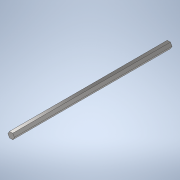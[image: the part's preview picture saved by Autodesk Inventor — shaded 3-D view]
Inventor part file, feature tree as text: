
AUTODESK INVENTOR PART (.ipt)
format: ipt  version: 2020 (Build 240168000, 168)  size: 103,424 bytes
history: native  units: in
note: dims shown in document units (in); Inventor stores cm internally (conversion verified against a paired STEP export)
features: extrude x1, sketch x1
ambient origin geometry x8: Origin, YZ Plane, XZ Plane, XY Plane, X Axis, Y Axis, Z Axis, Center Point
bodies: Solid1 (feature_tree)
feature tree (2):
  extrude  "Extrusion1"  Depth=14.0in TaperAngle=0.0deg
  sketch  "Sketch1"  dims[d0=0.5in d1=14.0in d2=0.0in]
